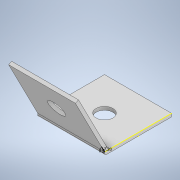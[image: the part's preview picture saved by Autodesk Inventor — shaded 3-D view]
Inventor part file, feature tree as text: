
AUTODESK INVENTOR PART (.ipt)
format: ipt  version: 2020.2 (Build 242310000, 310)  size: 138,752 bytes
history: native  units: in
note: dims shown in document units (in); Inventor stores cm internally (conversion verified against a paired STEP export)
features: sketch x6, extrude x5, plane x1, fillet x1
ambient origin geometry x8: Origin, YZ Plane, XZ Plane, XY Plane, X Axis, Y Axis, Z Axis, Center Point
bodies: Solid1 (feature_tree)
feature tree (13):
  extrude  "Extrusion1"  Depth=0.7874in
  sketch  "Sketch3"  dims[d2=0.0394in d3=0.0in d5=0.0787in]
  plane  "Work Plane1"
  extrude  "Extrusion2"  Depth=0.0394in
  extrude  "Extrusion3"  Depth=0.7874in
  fillet  "Fillet1"  Radius=0.7874in
  sketch  "Sketch6"  dims[d13=0.0197in d14=0.1969in]
  sketch  "Sketch7"  dims[d15=0.1969in d16=0.3937in d17=0.0in d18=0.3937in d19=0.0in]
  extrude  "Extrusion4"  Depth=0.7874in TaperAngle=0.0deg
  extrude  "Extrusion5"  Depth=0.0197in
  sketch  "Sketch1"  dims[d0=0.7874in d1=0.7874in]
  sketch  "Sketch4"  dims[d6=0.8053in d7=0.748in d8=0.7874in]
  sketch  "Sketch5"  dims[d9=0.0394in d10=0.0in d11=0.7874in d12=0.0in]
